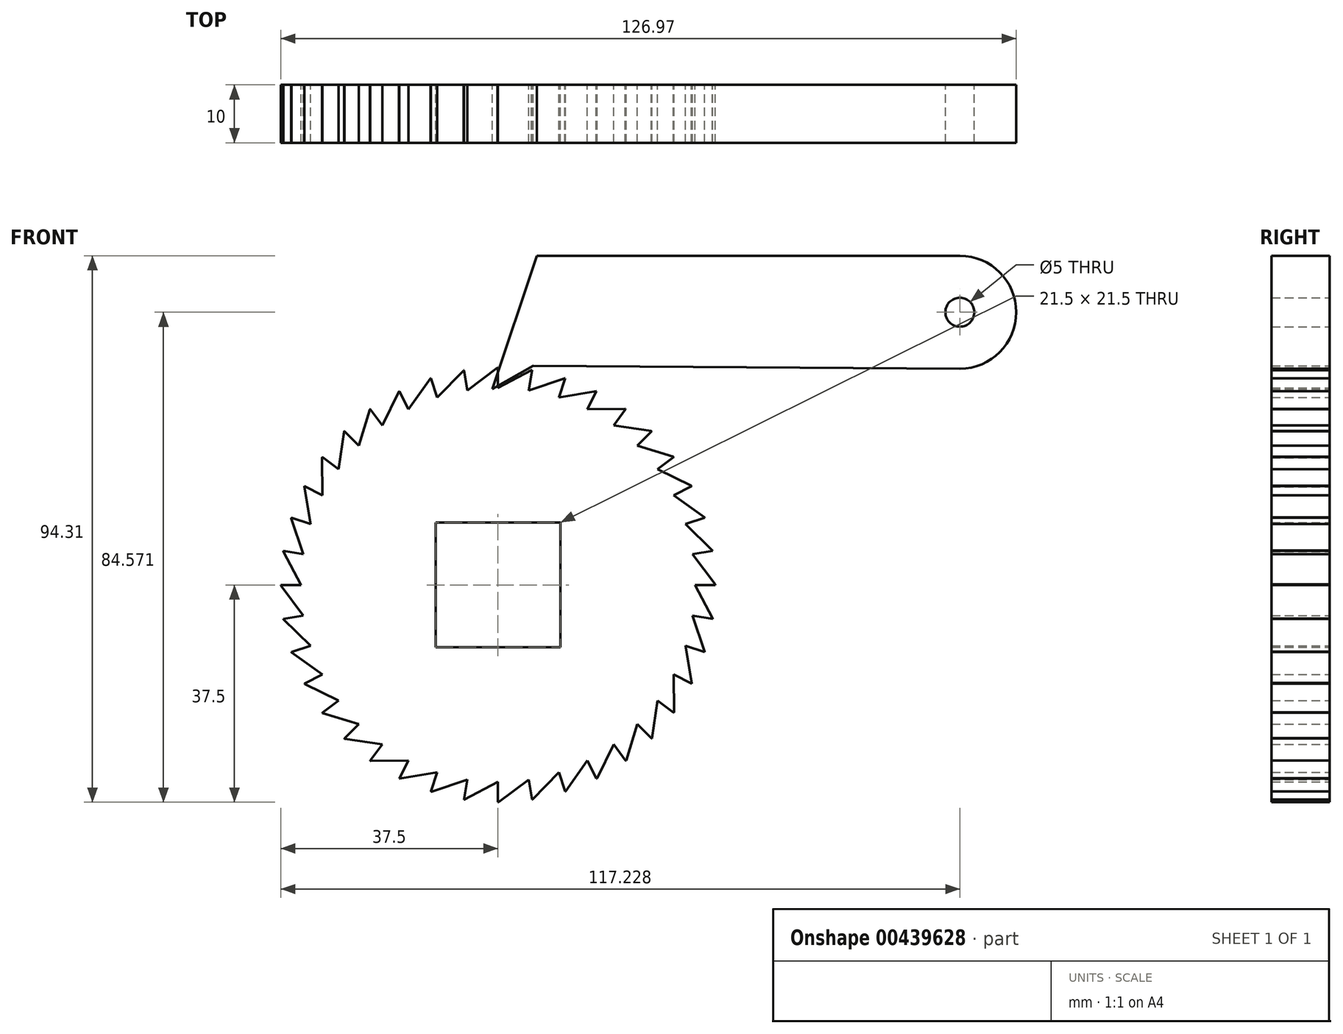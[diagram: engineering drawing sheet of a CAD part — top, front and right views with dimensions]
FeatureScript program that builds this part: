
annotation { "Feature Type Name" : "Feature", "Feature Type Description" : "" }
export const myFeature = defineFeature(function(context is Context, id is Id, definition is map)
    precondition{}
    {
        {
            var Q0;
            Q0=qCreatedBy(makeId("Front.planeOp"),FACE);
            var sketch = newSketch(context, id + "F0", { "sketchPlane" : qUnion([Q0])});
            skLineSegment(sketch, "E0.bottom", {"start": v(10.75, 10.75) * mm, "end": v(-10.75, 10.75) * mm});
            skLineSegment(sketch, "E0.top", {"start": v(10.75, -10.75) * mm, "end": v(-10.75, -10.75) * mm});
            skLineSegment(sketch, "E0.left", {"start": v(10.75, 10.75) * mm, "end": v(10.75, -10.75) * mm});
            skLineSegment(sketch, "E0.right", {"start": v(-10.75, 10.75) * mm, "end": v(-10.75, -10.75) * mm});
            skPoint(sketch, "E0.middle", {"position": v(0, 0) * mm});
            skCircle(sketch, "E1", {"center": v(0, 0) * mm, "radius": 37.5 * mm});
            skSolve(sketch);
        }
        {
            var Q0;
            Q0=makeQuery(id+"F0.imprint","IMPRINT",FACE,{"disambiguationData":[TD([[makeQuery(id+"F0.imprint","IMPRINT",EDGE,{"derivedFrom":sQuery(id+"F0.wireOp",EDGE,"E0.bottom")}),-1.0]])]});
            extrude(context, id + "F1", {"entities" : qUnion([Q0]), "depth" : 10 * mm});
        }
        {
            var Q0;
            Q0=qCreatedBy(makeId("Front.planeOp"),FACE);
            var sketch = newSketch(context, id + "F2", { "sketchPlane" : qUnion([Q0])});
            skLineSegment(sketch, "E2", {"start": v(0, 37.57) * mm, "end": v(0, 34) * mm});
            skLineSegment(sketch, "E3", {"start": v(0, 34) * mm, "end": v(5.88, 37.1) * mm});
            skLineSegment(sketch, "E4.1.0", {"start": v(-5.32, 33.59) * mm, "end": v(0, 37.57) * mm});
            skLineSegment(sketch, "E4.1.1", {"start": v(-5.88, 37.1) * mm, "end": v(-5.32, 33.59) * mm});
            skLineSegment(sketch, "E4.2.0", {"start": v(-10.5, 32.34) * mm, "end": v(-5.88, 37.1) * mm});
            skLineSegment(sketch, "E4.2.1", {"start": v(-11.6, 35.73) * mm, "end": v(-10.5, 32.34) * mm});
            skPoint(sketch, "E4.center", {"position": v(0, 0) * mm});
            skLineSegment(sketch, "E5.1.3.0", {"start": v(-15.44, 30.3) * mm, "end": v(-11.6, 35.73) * mm});
            skLineSegment(sketch, "E5.3.3.0", {"start": v(-17.05, 33.47) * mm, "end": v(-15.44, 30.3) * mm});
            skLineSegment(sketch, "E5.1.4.0", {"start": v(-19.99, 27.51) * mm, "end": v(-17.05, 33.47) * mm});
            skLineSegment(sketch, "E5.3.4.0", {"start": v(-22.08, 30.4) * mm, "end": v(-19.99, 27.51) * mm});
            skLineSegment(sketch, "E5.1.5.0", {"start": v(-24.05, 24.05) * mm, "end": v(-22.08, 30.4) * mm});
            skLineSegment(sketch, "E5.3.5.0", {"start": v(-26.56, 26.56) * mm, "end": v(-24.05, 24.05) * mm});
            skLineSegment(sketch, "E5.1.6.0", {"start": v(-27.51, 19.99) * mm, "end": v(-26.56, 26.56) * mm});
            skLineSegment(sketch, "E5.3.6.0", {"start": v(-30.4, 22.08) * mm, "end": v(-27.51, 19.99) * mm});
            skLineSegment(sketch, "E5.1.7.0", {"start": v(-30.3, 15.44) * mm, "end": v(-30.4, 22.08) * mm});
            skLineSegment(sketch, "E5.3.7.0", {"start": v(-33.47, 17.05) * mm, "end": v(-30.3, 15.44) * mm});
            skLineSegment(sketch, "E5.1.8.0", {"start": v(-32.34, 10.5) * mm, "end": v(-33.47, 17.05) * mm});
            skLineSegment(sketch, "E5.3.8.0", {"start": v(-35.73, 11.6) * mm, "end": v(-32.34, 10.5) * mm});
            skLineSegment(sketch, "E5.1.9.0", {"start": v(-33.59, 5.32) * mm, "end": v(-35.73, 11.6) * mm});
            skLineSegment(sketch, "E5.3.9.0", {"start": v(-37.1, 5.88) * mm, "end": v(-33.59, 5.32) * mm});
            skLineSegment(sketch, "E5.1.10.0", {"start": v(-34, 0) * mm, "end": v(-37.1, 5.88) * mm});
            skLineSegment(sketch, "E5.3.10.0", {"start": v(-37.57, 0) * mm, "end": v(-34, 0) * mm});
            skLineSegment(sketch, "E5.1.11.0", {"start": v(-33.59, -5.32) * mm, "end": v(-37.57, 0) * mm});
            skLineSegment(sketch, "E5.3.11.0", {"start": v(-37.1, -5.88) * mm, "end": v(-33.59, -5.32) * mm});
            skLineSegment(sketch, "E5.1.12.0", {"start": v(-32.34, -10.5) * mm, "end": v(-37.1, -5.88) * mm});
            skLineSegment(sketch, "E5.3.12.0", {"start": v(-35.73, -11.6) * mm, "end": v(-32.34, -10.5) * mm});
            skLineSegment(sketch, "E5.1.13.0", {"start": v(-30.3, -15.44) * mm, "end": v(-35.73, -11.6) * mm});
            skLineSegment(sketch, "E5.3.13.0", {"start": v(-33.47, -17.05) * mm, "end": v(-30.3, -15.44) * mm});
            skLineSegment(sketch, "E5.1.14.0", {"start": v(-27.51, -19.99) * mm, "end": v(-33.47, -17.05) * mm});
            skLineSegment(sketch, "E5.3.14.0", {"start": v(-30.4, -22.08) * mm, "end": v(-27.51, -19.99) * mm});
            skLineSegment(sketch, "E5.1.15.0", {"start": v(-24.05, -24.05) * mm, "end": v(-30.4, -22.08) * mm});
            skLineSegment(sketch, "E5.3.15.0", {"start": v(-26.56, -26.56) * mm, "end": v(-24.05, -24.05) * mm});
            skLineSegment(sketch, "E5.1.16.0", {"start": v(-19.99, -27.51) * mm, "end": v(-26.56, -26.56) * mm});
            skLineSegment(sketch, "E5.3.16.0", {"start": v(-22.08, -30.4) * mm, "end": v(-19.99, -27.51) * mm});
            skLineSegment(sketch, "E5.1.17.0", {"start": v(-15.44, -30.3) * mm, "end": v(-22.08, -30.4) * mm});
            skLineSegment(sketch, "E5.3.17.0", {"start": v(-17.05, -33.47) * mm, "end": v(-15.44, -30.3) * mm});
            skLineSegment(sketch, "E5.1.18.0", {"start": v(-10.5, -32.34) * mm, "end": v(-17.05, -33.47) * mm});
            skLineSegment(sketch, "E5.3.18.0", {"start": v(-11.6, -35.73) * mm, "end": v(-10.5, -32.34) * mm});
            skLineSegment(sketch, "E5.1.19.0", {"start": v(-5.32, -33.59) * mm, "end": v(-11.6, -35.73) * mm});
            skLineSegment(sketch, "E5.3.19.0", {"start": v(-5.88, -37.1) * mm, "end": v(-5.32, -33.59) * mm});
            skLineSegment(sketch, "E6.1.20.0", {"start": v(0, -34) * mm, "end": v(-5.88, -37.1) * mm});
            skLineSegment(sketch, "E6.3.20.0", {"start": v(0, -37.57) * mm, "end": v(0, -34) * mm});
            skLineSegment(sketch, "E6.1.21.0", {"start": v(5.32, -33.59) * mm, "end": v(0, -37.57) * mm});
            skLineSegment(sketch, "E6.3.21.0", {"start": v(5.88, -37.1) * mm, "end": v(5.32, -33.59) * mm});
            skLineSegment(sketch, "E6.1.22.0", {"start": v(10.5, -32.34) * mm, "end": v(5.88, -37.1) * mm});
            skLineSegment(sketch, "E6.3.22.0", {"start": v(11.6, -35.73) * mm, "end": v(10.5, -32.34) * mm});
            skLineSegment(sketch, "E6.1.23.0", {"start": v(15.44, -30.3) * mm, "end": v(11.6, -35.73) * mm});
            skLineSegment(sketch, "E6.3.23.0", {"start": v(17.05, -33.47) * mm, "end": v(15.44, -30.3) * mm});
            skLineSegment(sketch, "E6.1.24.0", {"start": v(19.99, -27.51) * mm, "end": v(17.05, -33.47) * mm});
            skLineSegment(sketch, "E6.3.24.0", {"start": v(22.08, -30.4) * mm, "end": v(19.99, -27.51) * mm});
            skLineSegment(sketch, "E7.1.25.0", {"start": v(24.05, -24.05) * mm, "end": v(22.08, -30.4) * mm});
            skLineSegment(sketch, "E7.3.25.0", {"start": v(26.56, -26.56) * mm, "end": v(24.05, -24.05) * mm});
            skLineSegment(sketch, "E7.1.26.0", {"start": v(27.51, -19.99) * mm, "end": v(26.56, -26.56) * mm});
            skLineSegment(sketch, "E7.3.26.0", {"start": v(30.4, -22.08) * mm, "end": v(27.51, -19.99) * mm});
            skLineSegment(sketch, "E7.1.27.0", {"start": v(30.3, -15.44) * mm, "end": v(30.4, -22.08) * mm});
            skLineSegment(sketch, "E7.3.27.0", {"start": v(33.47, -17.05) * mm, "end": v(30.3, -15.44) * mm});
            skLineSegment(sketch, "E7.1.28.0", {"start": v(32.34, -10.5) * mm, "end": v(33.47, -17.05) * mm});
            skLineSegment(sketch, "E7.3.28.0", {"start": v(35.73, -11.6) * mm, "end": v(32.34, -10.5) * mm});
            skLineSegment(sketch, "E7.1.29.0", {"start": v(33.59, -5.32) * mm, "end": v(35.73, -11.6) * mm});
            skLineSegment(sketch, "E7.3.29.0", {"start": v(37.1, -5.88) * mm, "end": v(33.59, -5.32) * mm});
            skLineSegment(sketch, "E8.1.30.0", {"start": v(34, 0) * mm, "end": v(37.1, -5.88) * mm});
            skLineSegment(sketch, "E8.3.30.0", {"start": v(37.57, 0) * mm, "end": v(34, 0) * mm});
            skLineSegment(sketch, "E8.1.31.0", {"start": v(33.59, 5.32) * mm, "end": v(37.57, 0) * mm});
            skLineSegment(sketch, "E8.3.31.0", {"start": v(37.1, 5.88) * mm, "end": v(33.59, 5.32) * mm});
            skLineSegment(sketch, "E9.1.32.0", {"start": v(32.34, 10.5) * mm, "end": v(37.1, 5.88) * mm});
            skLineSegment(sketch, "E9.3.32.0", {"start": v(35.73, 11.6) * mm, "end": v(32.34, 10.5) * mm});
            skLineSegment(sketch, "E9.1.33.0", {"start": v(30.3, 15.44) * mm, "end": v(35.73, 11.6) * mm});
            skLineSegment(sketch, "E9.3.33.0", {"start": v(33.47, 17.05) * mm, "end": v(30.3, 15.44) * mm});
            skLineSegment(sketch, "E9.1.34.0", {"start": v(27.51, 19.99) * mm, "end": v(33.47, 17.05) * mm});
            skLineSegment(sketch, "E9.3.34.0", {"start": v(30.4, 22.08) * mm, "end": v(27.51, 19.99) * mm});
            skLineSegment(sketch, "E9.1.35.0", {"start": v(24.05, 24.05) * mm, "end": v(30.4, 22.08) * mm});
            skLineSegment(sketch, "E9.3.35.0", {"start": v(26.56, 26.56) * mm, "end": v(24.05, 24.05) * mm});
            skLineSegment(sketch, "E9.1.36.0", {"start": v(19.99, 27.51) * mm, "end": v(26.56, 26.56) * mm});
            skLineSegment(sketch, "E9.3.36.0", {"start": v(22.08, 30.4) * mm, "end": v(19.99, 27.51) * mm});
            skLineSegment(sketch, "E9.1.37.0", {"start": v(15.44, 30.3) * mm, "end": v(22.08, 30.4) * mm});
            skLineSegment(sketch, "E9.3.37.0", {"start": v(17.05, 33.47) * mm, "end": v(15.44, 30.3) * mm});
            skLineSegment(sketch, "E9.1.38.0", {"start": v(10.5, 32.34) * mm, "end": v(17.05, 33.47) * mm});
            skLineSegment(sketch, "E9.3.38.0", {"start": v(11.6, 35.73) * mm, "end": v(10.5, 32.34) * mm});
            skLineSegment(sketch, "E9.1.39.0", {"start": v(5.32, 33.59) * mm, "end": v(11.6, 35.73) * mm});
            skLineSegment(sketch, "E9.3.39.0", {"start": v(5.88, 37.1) * mm, "end": v(5.32, 33.59) * mm});
            skSolve(sketch);
        }
        {
            var Q0;
            Q0=makeQuery(id+"F2.imprint","IMPRINT",FACE,{"disambiguationData":[TD([[makeQuery(id+"F2.imprint","IMPRINT",EDGE,{"derivedFrom":sQuery(id+"F2.wireOp",EDGE,"E2")}),-1.0]])]});
            extrude(context, id + "F3", {"entities" : qUnion([Q0]), "operationType" : NewBodyOperationType.INTERSECT, "depth" : 25 * mm});
        }
        {
            var Q0;
            Q0=qCreatedBy(makeId("Front.planeOp"),FACE);
            var sketch = newSketch(context, id + "F4", { "sketchPlane" : qUnion([Q0])});
            skLineSegment(sketch, "E10", {"start": v(6.69, 56.8) * mm, "end": v(8.7, 56.8) * mm});
            skLineSegment(sketch, "E11", {"start": v(8.7, 56.8) * mm, "end": v(79.73, 56.8) * mm});
            skArc(sketch, "E12", {"start": v(79.73, 37.33) * mm, "mid": v(89.47, 47.07) * mm, "end": v(79.73, 56.8) * mm});
            skLineSegment(sketch, "E13", {"start": v(-1, 33.8) * mm, "end": v(6.09, 37.82) * mm});
            skLineSegment(sketch, "E14", {"start": v(6.09, 37.82) * mm, "end": v(79.73, 37.33) * mm});
            skLineSegment(sketch, "E15", {"start": v(-1, 33.8) * mm, "end": v(6.69, 56.8) * mm});
            skCircle(sketch, "E16", {"center": v(79.73, 47.07) * mm, "radius": 2.5 * mm});
            skSolve(sketch);
        }
        {
            var Q0;
            Q0=makeQuery(id+"F4.imprint","IMPRINT",FACE,{"disambiguationData":[TD([[makeQuery(id+"F4.imprint","IMPRINT",EDGE,{"derivedFrom":sQuery(id+"F4.wireOp",EDGE,"E10")}),-1.0]])]});
            extrude(context, id + "F5", {"entities" : qUnion([Q0]), "depth" : 10 * mm});
        }
    });
